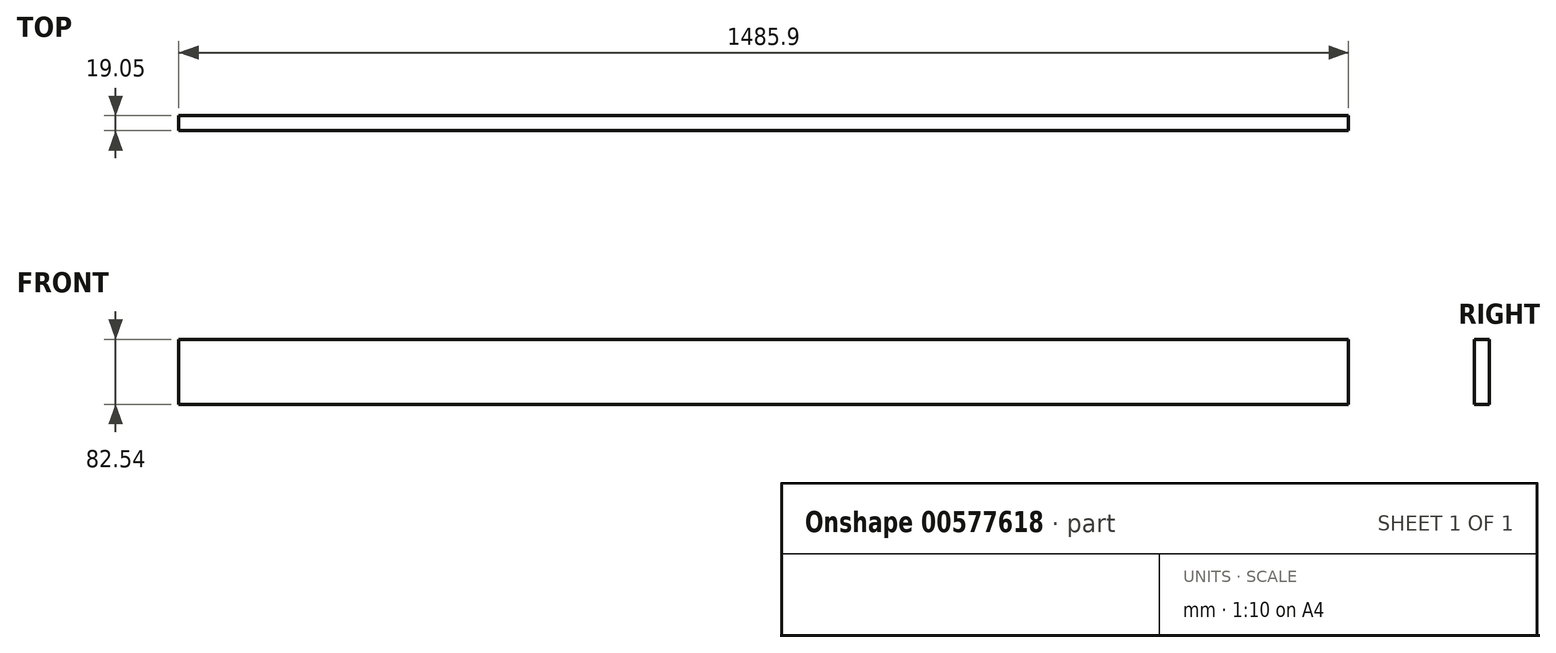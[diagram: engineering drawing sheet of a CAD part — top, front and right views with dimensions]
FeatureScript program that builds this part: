
annotation { "Feature Type Name" : "Feature", "Feature Type Description" : "" }
export const myFeature = defineFeature(function(context is Context, id is Id, definition is map)
    precondition{}
    {
        {
            var Q0;
            Q0=qCreatedBy(makeId("Front.planeOp"),FACE);
            var sketch = newSketch(context, id + "F0", { "sketchPlane" : qUnion([Q0])});
            skLineSegment(sketch, "E0.bottom", {"start": v(742.95, 41.28) * mm, "end": v(-742.95, 41.27) * mm});
            skLineSegment(sketch, "E0.top", {"start": v(742.95, -41.27) * mm, "end": v(-742.95, -41.28) * mm});
            skLineSegment(sketch, "E0.left", {"start": v(742.95, 41.28) * mm, "end": v(742.95, -41.27) * mm});
            skLineSegment(sketch, "E0.right", {"start": v(-742.95, 41.27) * mm, "end": v(-742.95, -41.28) * mm});
            skPoint(sketch, "E0.middle", {"position": v(0, 0) * mm});
            skSolve(sketch);
        }
        {
            var Q0;
            Q0=makeQuery(id+"F0.imprint","IMPRINT",FACE,{"disambiguationData":[TD([[makeQuery(id+"F0.imprint","IMPRINT",EDGE,{"derivedFrom":sQuery(id+"F0.wireOp",EDGE,"E0.bottom")}),1.0]])]});
            extrude(context, id + "F1", {"entities" : qUnion([Q0]), "depth" : 19.05 * mm, "offsetDistance" : 25.4 * mm});
        }
    });
